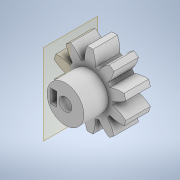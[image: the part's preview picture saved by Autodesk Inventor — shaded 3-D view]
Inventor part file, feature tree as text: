
AUTODESK INVENTOR PART (.ipt)
format: ipt  version: 2020 (Build 240168000, 168)  size: 212,992 bytes
history: native  units: in
note: dims shown in document units (in); Inventor stores cm internally (conversion verified against a paired STEP export)
features: extrude x5, sketch x5, other x2, plane x1
ambient origin geometry x8: Origin, YZ Plane, XZ Plane, XY Plane, X Axis, Y Axis, Z Axis, Center Point
bodies: Solid1 (feature_tree)
feature tree (13):
  extrude  "Extrusion1"  Depth=0.3937in
  other  "Spur Gear Teeth1"
  extrude  "Extrusion2"  Depth=0.3937in TaperAngle=0.0deg
  extrude  "Extrusion3"  Depth=0.3937in TaperAngle=0.0deg
  plane  "Work Plane1"
  extrude  "Extrusion5"  Depth=0.1181in
  extrude  "Extrusion6"  Depth=0.3937in TaperAngle=0.0deg
  sketch  "Sketch1"  dims[d0=0.3937in d1=0.0in d2=1.9685in]
  other  "Spur Gear1"
  sketch  "Sketch2"  dims[d3=0.5906in d4=0.3937in d5=0.0in]
  sketch  "Sketch3"  dims[d6=0.2047in d7=0.3937in d8=0.0in]
  sketch  "Sketch5"  dims[d11=-0.3125in d12=0.1181in]
  sketch  "Sketch6"  dims[d13=0.5906in d14=0.3937in d15=0.0in d17=0.0984in d19=0.1083in d20=0.2165in d21=0.2953in d22=0.0in]
